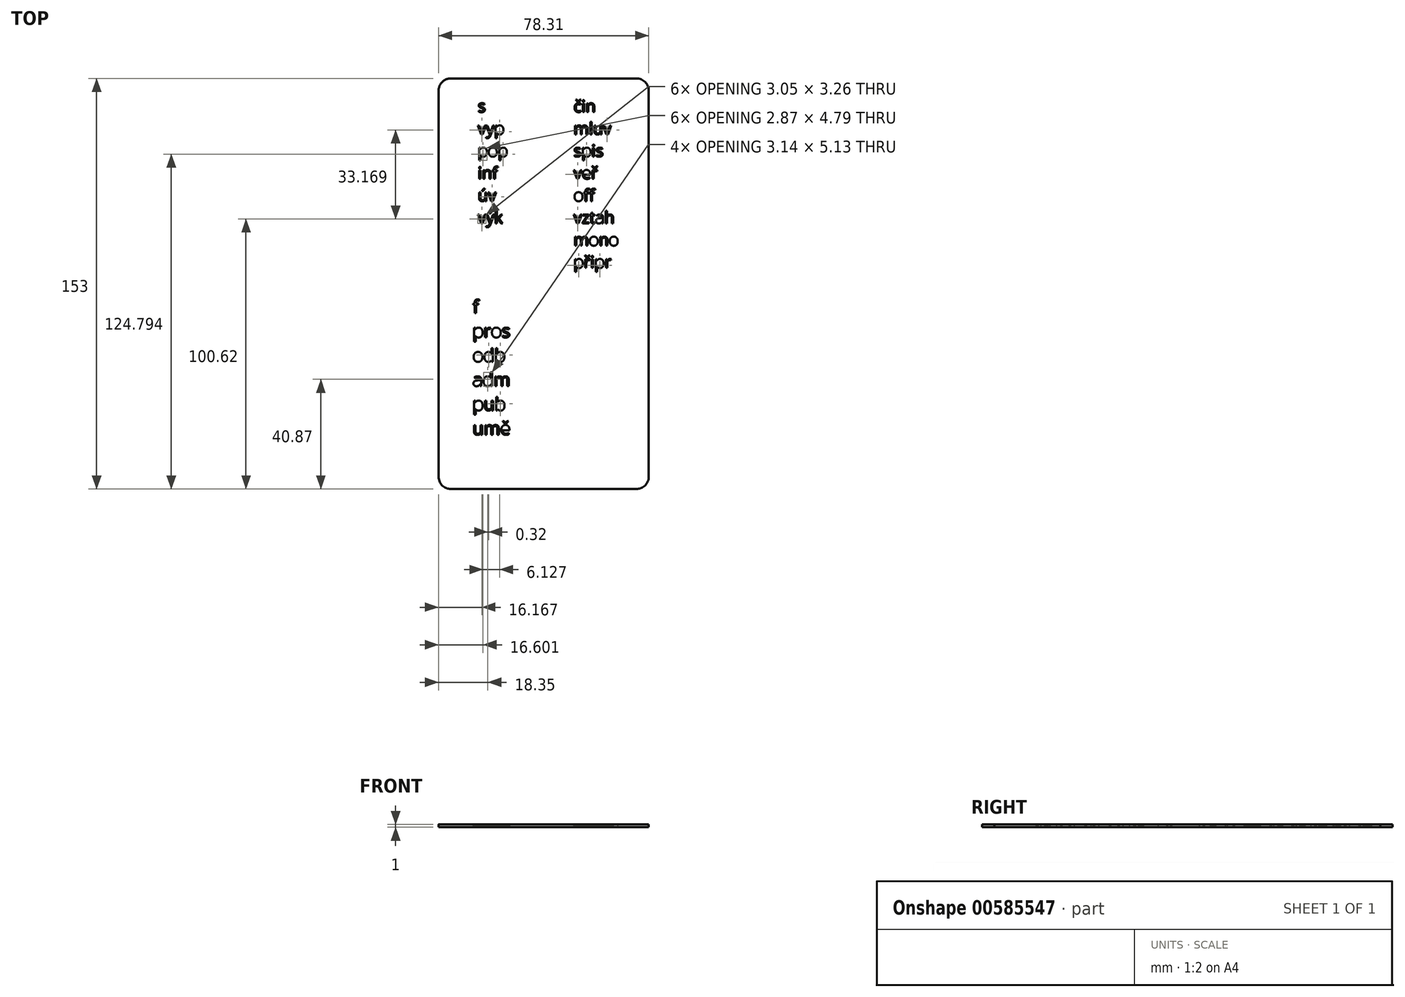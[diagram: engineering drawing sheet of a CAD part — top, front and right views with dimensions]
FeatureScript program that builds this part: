
annotation { "Feature Type Name" : "Feature", "Feature Type Description" : "" }
export const myFeature = defineFeature(function(context is Context, id is Id, definition is map)
    precondition{}
    {
        {
            var Q0;
            Q0=qCreatedBy(makeId("Top.planeOp"),FACE);
            var sketch = newSketch(context, id + "F0", { "sketchPlane" : qUnion([Q0])});
            skLineSegment(sketch, "E0", {"start": v(-28.8, -60.1) * mm, "end": v(40.3, -60.1) * mm});
            skLineSegment(sketch, "E1", {"start": v(-33.4, -55.5) * mm, "end": v(-33.4, 88.51) * mm});
            skLineSegment(sketch, "E2", {"start": v(-28.8, 92.9) * mm, "end": v(40.3, 92.9) * mm});
            skLineSegment(sketch, "E3", {"start": v(44.9, 88.3) * mm, "end": v(44.9, -55.5) * mm});
            skLineSegment(sketch, "E4", {"start": v(-33.4, 16.4) * mm, "end": v(44.9, 16.4) * mm});
            skLineSegment(sketch, "E5", {"start": v(5.76, 92.9) * mm, "end": v(5.76, 16.4) * mm});
            skLineSegment(sketch, "E6", {"start": v(5.76, 16.4) * mm, "end": v(5.76, -60.1) * mm});
            skText(sketch, "E7", { "text": "s\nvyp\npop\ninf\núv\nvýk", "fontName": "OpenSans-Regular.ttf"});
            skText(sketch, "E8", { "text": "f\npros\nodb\nadm\npub\numě", "fontName": "OpenSans-Regular.ttf"});
            skText(sketch, "E9", { "text": "čin\nmluv\nspis\nveř\noff\nvztah\nmono\npřipr", "fontName": "OpenSans-Regular.ttf"});
            skLineSegment(sketch, "E10", {"start": v(-33.4, 88.51) * mm, "end": v(-33.4, 88.3) * mm});
            skLineSegment(sketch, "E11", {"start": v(-28.8, 88.3) * mm, "end": v(40.3, 88.3) * mm});
            skArc(sketch, "E12", {"start": v(44.9, 88.3) * mm, "mid": v(43.55, 91.55) * mm, "end": v(40.3, 92.9) * mm});
            skPoint(sketch, "E13.end.orphan", {"position": v(44.9, 92.9) * mm});
            skLineSegment(sketch, "E14.trimOffspring", {"start": v(44.9, 88.3) * mm, "end": v(44.9, 88.3) * mm});
            skArc(sketch, "E15", {"start": v(-28.8, 92.9) * mm, "mid": v(-32.12, 91.47) * mm, "end": v(-33.4, 88.08) * mm});
            skPoint(sketch, "E16.orphan", {"position": v(-33.4, 92.9) * mm});
            skCircle(sketch, "E17", {"center": v(-28.8, -55.5) * mm, "radius": 4.6 * mm});
            skArc(sketch, "E18", {"start": v(40.3, -60.1) * mm, "mid": v(43.55, -58.75) * mm, "end": v(44.9, -55.5) * mm});
            skPoint(sketch, "E19.orphan", {"position": v(44.9, -60.1) * mm});
            skLineSegment(sketch, "E20", {"start": v(44.9, -55.5) * mm, "end": v(44.9, -55.5) * mm});
            skPoint(sketch, "E21.end.orphan", {"position": v(-33.4, -55.5) * mm});
            skPoint(sketch, "E22.orphan", {"position": v(-33.4, -60.1) * mm});
            skLineSegment(sketch, "E23", {"start": v(-28.8, -55.5) * mm, "end": v(-28.8, -60.1) * mm});
            const initialGuessF0  = {"E7": [-0.01876, 0.08035, 1, 0, 0.00439], "E8": [-0.0207, 0.00547, 1, 0, 0.0048], "E9": [0.01692, 0.08035, 1, 0, 0.00439]};
            skSetInitialGuess(sketch, initialGuessF0);
            skSolve(sketch);
        }
        {
            var Q0;
            Q0 = qSketchRegion(id + "F0", true);
            extrude(context, id + "F1", {"entities" : qUnion([Q0]), "depth" : 1 * mm, "offsetDistance" : 25 * mm});
        }
    });
